# Revit family: Urinal-Wall_Mount-KOHLER-Portico-K-38020T-1
name_source: partatom
category: Plumbing Fixtures
units: mm (PartAtom-declared; Revit-internal decimal feet)

## family parameters
Cut with Voids When Loaded = No
Host = Face
OmniClass Number = 23.31.21.00
OmniClass Title = Urinals
Part Type = Normal
Room Calculation Point = No
Round Connector Dimension = Use Diameter
Shared = No

## types (2) — shared parameters
ADA Compliant = No
Assembly Code = D2010200
CW Connection = Yes
Cold Water Inlet = Cold Water Inlet
Date Modified = 05/25/2024
Default Elevation = 0"
Description = Padi Wall Mounted Super Water-Saving Urinal (Rear Water Inlet) (0.5L/1L/2.5L)
Flow Rate = 0 GPM
Flush Rate- GPF = 0.66GPF
Flush Rate- LPF = 2.5LPF
HW Connection = No
Height = 26 13/16"
Hot Water Inlet = Hot Water Inlet
Length = 14 3/16"
Manufacturer = Kohler Co.
Master Format 2014 = 22 41 13.16
Master Format 2014 Name = Residential Urinals
Material = Vitreous China
Pressure = 0.00 psi
Product Documentation Link = https://files.kohler.com.cn
Product Name = Portico
URL = http://www.kohler.com.cn
Vent Connection = No
Waste Connection = Yes
Waste Water Outlet = Waste Water Outlet
WaterSense Certified = No
Width = 15 1/4"

## per-type parameters (varying)
| type | Finish | Model | Product Page URL | Type |
| 0-White | Kohler-Vitreous_China-0-White | K-38020T-ER-0 | https://www.kohler.com.cn | 1 |
| 7-Black Black | Kohler-Vitreous_China-7-Black_Black | K-38020T-ER-7 |  | 2 |

## geometry (parser evidence)
native form markers: Sweep x5
no freeform markers — native parametric forms only
